# Revit family: WashbasinUnit-100cm-WithDoors-Vitra-SentoSeries-60787+60799+60811
name_source: partatom
category: Furniture Systems
revit_build: Autodesk Revit 2017 (Build: 20160225_1515(x64)
units: mm (PartAtom-declared; Revit-internal decimal feet)

## family parameters
Cut with Voids When Loaded = No
Host = Face
OmniClass Number = 23.40.00.00
OmniClass Title = Equipment and Furnishings
Part Type = Normal
Room Calculation Point = No
Round Connector Dimension = Use Diameter
Shared = Yes

## types (6) — shared parameters
Ambience Led Lighting = 220V
BIMobject category = Bathroom compound units
Construction Type = Face Mounted
Default Elevation = 705 mm  [stored 2.31299 ft]
Depth(mm) = 340 mm  [stored 1.11549 ft]
Design country = Turkey
Height(mm) = 780 mm  [stored 2.55906 ft]
IFC Classification = Furniture
Manufacturer = Vitra
Manufacturer name = Vitra
Masterformat 2014 Code = 13 42 13
Masterformat 2014 Description = Bathroom Unit Modules
NBS Referans Code = 35-75-08
NBS Referans Description = Bathroom Cabinets
Nominal height = 0.000
Nominal width = 0.000
OmniClass Code = 23-31 25 13
OmniClass Description = Bathroom Cabinets
Primary Material = oak
Product certification = https://vitraglobal.com
Product data url = https://www.vitraglobal.com
Product family = Sento
Product group = Washbasin Unit
UNSPSC Code = 301815
UNSPSC Description = Bathroom Cabinets
URL = https://vitraglobal.com
Uniclass 1.4 Code = L8241
Uniclass 1.4 Description = Bathroom Cabinets
Uniclass 2.0 Code = PR-35-75-08
Uniclass 2.0 Description = Bathroom Cabinets
Uniclass 2015 Code = Pr_40_20_93
Uniclass 2015 Name = Wash basins, sinks and troughs
Uniformat II Code = E20
Uniformat II Description = FURNISHINGS
Warranty Period (Year) = 2
Width(mm) = 900 mm  [stored 2.95276 ft]
With 1 Drawer = No
With door = Yes
Youtube = https://www.youtube.com

## per-type parameters (varying)
| type | Article No. (default) | Description | Model | Product SKU | Secondary Material | Technical description | Weight Net (kg) | Without legs |
| Sento Washbasin Unit, 100cm, with doors, without legs, Matte White-60787 | 60787 | Sento Washbasin Unit, 100 cm, with doors, without legs | 60787 | 60787 | MatteWhite | https://www.vitra.com.tr | 66,000 | No |
| Sento Washbasin Unit, 100cm, with doors, without legs, MatteAnthracite-60811 | 60811 | Sento Washbasin Unit, 100 cm, with doors, without legs | 60811 | 60811 | Matte Antrasit | https://www.vitra.com.tr | 54,000 | No |
| Sento Washbasin Unit, 100cm, with doors, without legs, MatteCream-60799 | 60799 | Sento Washbasin Unit, 100 cm, with doors, without legs | 60799 | 60799 | Matte Cream | https://www.vitra.com.tr | 54,000 | No |
| Sento Washbasin Unit, 100cm, with doors, with legs, Matte White-60786 | 60786 | Sento Washbasin Unit, 100 cm, with doors, with legs | 60786 | 60786 | MatteWhite |  | 54,000 | Yes |
| Sento Washbasin Unit, 100cm, with doors, with legs, MatteAnthracite-60810 | 60810 | Sento Washbasin Unit, 100 cm, with doors, with legs | 60810 | 60810 | Matte Antrasit |  | 54,000 | Yes |
| Sento Washbasin Unit, 100cm, with doors, with legs, MatteCream-60798 | 60798 | Sento Washbasin Unit, 100 cm, with doors, with legs | 60798 | 60798 | Matte Cream |  | 54,000 | Yes |

note: [stored X ft] marks values corroborated as IEEE doubles in the binary element streams (Revit-internal decimal feet)

## geometry (parser evidence)
native form markers: Sweep x2
no freeform markers — native parametric forms only
